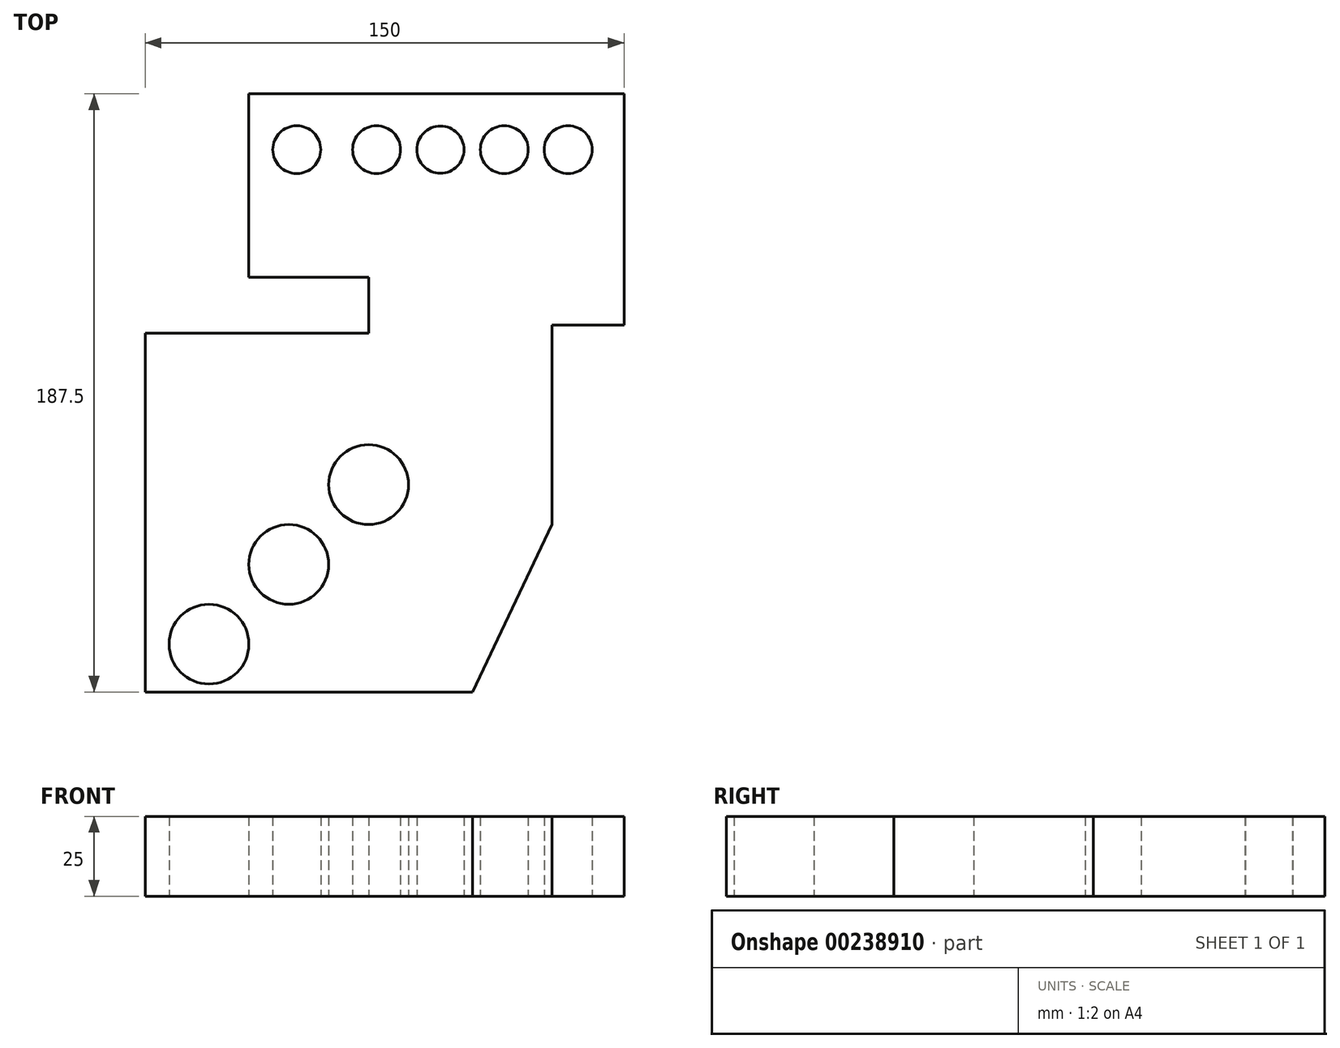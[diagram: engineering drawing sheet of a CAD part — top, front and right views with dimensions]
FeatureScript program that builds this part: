
annotation { "Feature Type Name" : "Feature", "Feature Type Description" : "" }
export const myFeature = defineFeature(function(context is Context, id is Id, definition is map)
    precondition{}
    {
        {
            var Q0;
            Q0=qCreatedBy(makeId("Top.planeOp"),FACE);
            var sketch = newSketch(context, id + "F0", { "sketchPlane" : qUnion([Q0])});
            skLineSegment(sketch, "E0", {"start": v(-57.64, -72.55) * mm, "end": v(44.86, -72.55) * mm});
            skLineSegment(sketch, "E1", {"start": v(-57.64, -72.55) * mm, "end": v(-57.64, 39.95) * mm});
            skLineSegment(sketch, "E2", {"start": v(-57.64, 39.95) * mm, "end": v(12.36, 39.95) * mm});
            skLineSegment(sketch, "E3", {"start": v(12.36, 39.95) * mm, "end": v(12.36, 57.45) * mm});
            skLineSegment(sketch, "E4", {"start": v(12.36, 57.45) * mm, "end": v(-25.14, 57.45) * mm});
            skLineSegment(sketch, "E5", {"start": v(-25.14, 57.45) * mm, "end": v(-25.14, 114.95) * mm});
            skLineSegment(sketch, "E6", {"start": v(-25.14, 114.95) * mm, "end": v(92.36, 114.95) * mm});
            skLineSegment(sketch, "E7", {"start": v(92.36, 114.95) * mm, "end": v(92.36, 42.45) * mm});
            skLineSegment(sketch, "E8", {"start": v(92.36, 42.45) * mm, "end": v(69.86, 42.45) * mm});
            skLineSegment(sketch, "E9", {"start": v(69.86, 42.45) * mm, "end": v(69.86, -20.05) * mm});
            skLineSegment(sketch, "E10", {"start": v(69.86, -20.05) * mm, "end": v(44.86, -72.55) * mm});
            skCircle(sketch, "E11", {"center": v(-37.64, -57.55) * mm, "radius": 12.5 * mm});
            skCircle(sketch, "E12", {"center": v(-12.64, -32.55) * mm, "radius": 12.5 * mm});
            skCircle(sketch, "E13", {"center": v(12.36, -7.55) * mm, "radius": 12.5 * mm});
            skCircle(sketch, "E14", {"center": v(-10.14, 97.45) * mm, "radius": 7.5 * mm});
            skCircle(sketch, "E15", {"center": v(14.86, 97.45) * mm, "radius": 7.5 * mm});
            skCircle(sketch, "E16", {"center": v(34.86, 97.45) * mm, "radius": 7.4 * mm});
            skCircle(sketch, "E17", {"center": v(54.86, 97.45) * mm, "radius": 7.5 * mm});
            skCircle(sketch, "E18", {"center": v(74.86, 97.45) * mm, "radius": 7.5 * mm});
            skSolve(sketch);
        }
        {
            var Q0;
            Q0 = qSketchRegion(id + "F0", true);
            extrude(context, id + "F1", {"entities" : qUnion([Q0]), "depth" : 25 * mm});
        }
    });
